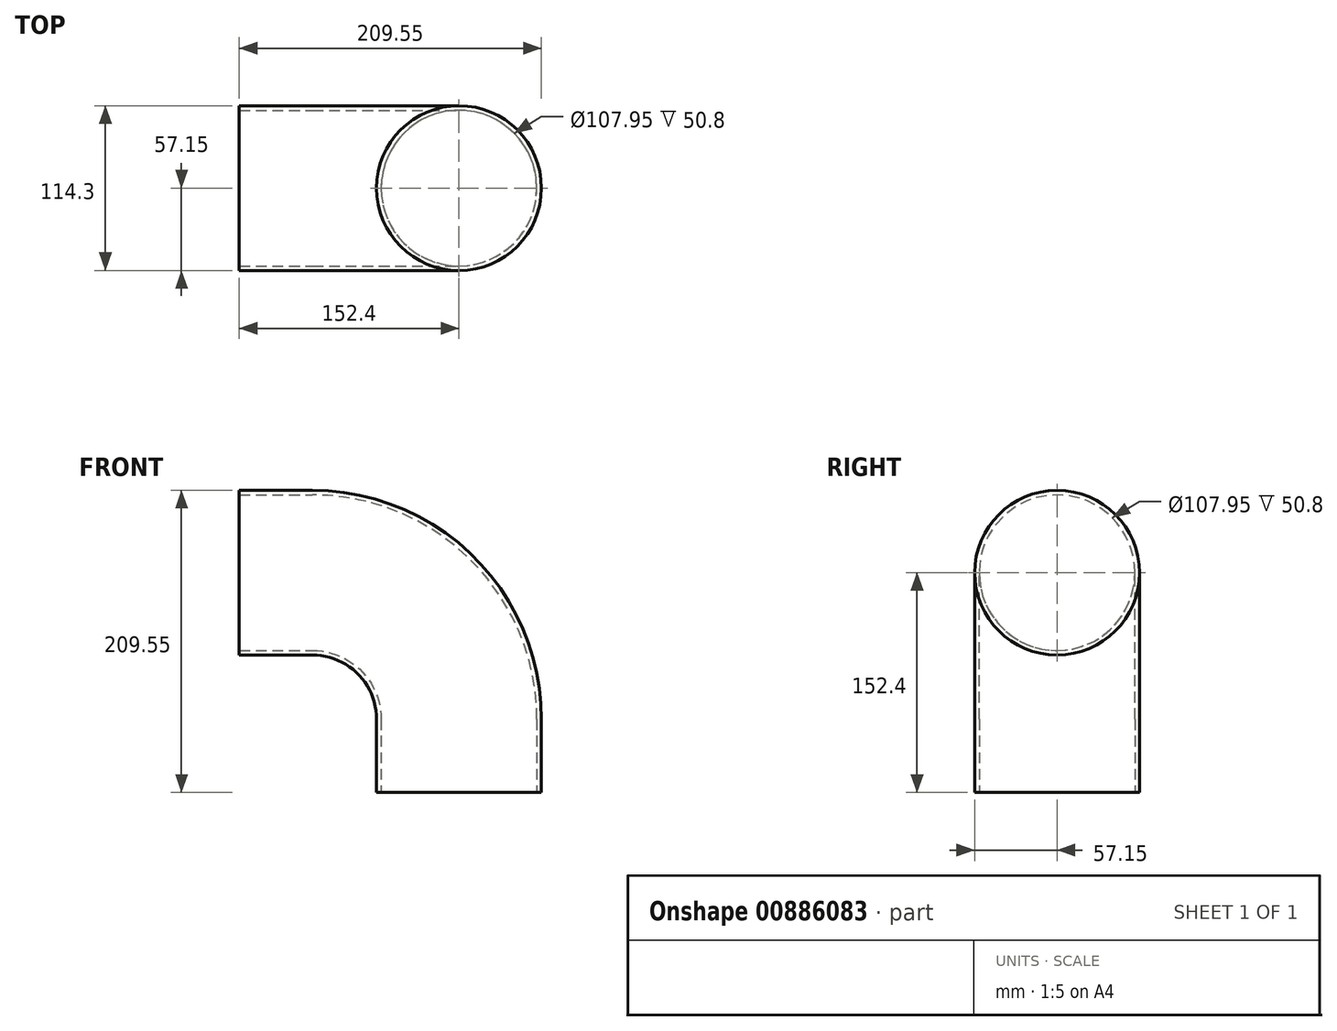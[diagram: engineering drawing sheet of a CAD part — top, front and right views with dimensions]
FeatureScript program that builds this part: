
annotation { "Feature Type Name" : "Feature", "Feature Type Description" : "" }
export const myFeature = defineFeature(function(context is Context, id is Id, definition is map)
    precondition{}
    {
        {
            var Q0;
            Q0=qCreatedBy(makeId("Front.planeOp"),FACE);
            var sketch = newSketch(context, id + "F0", { "sketchPlane" : qUnion([Q0])});
            skLineSegment(sketch, "E0", {"start": v(0, 0) * mm, "end": v(50.8, 0) * mm});
            skLineSegment(sketch, "E1", {"start": v(152.4, -101.6) * mm, "end": v(152.4, -152.4) * mm});
            skPoint(sketch, "E2.visualSharp", {"position": v(152.4, 0) * mm});
            skArc(sketch, "E2.filletArc", {"start": v(152.4, -101.6) * mm, "mid": v(122.64, -29.76) * mm, "end": v(50.8, 0) * mm});
            skSolve(sketch);
        }
        {
            var Q0;
            Q0=qCreatedBy(makeId("Right.planeOp"),FACE);
            var sketch = newSketch(context, id + "F1", { "sketchPlane" : qUnion([Q0])});
            skCircle(sketch, "E3", {"center": v(0, 0) * mm, "radius": 53.98 * mm});
            skCircle(sketch, "E4", {"center": v(0, 0) * mm, "radius": 57.15 * mm});
            skSolve(sketch);
        }
        {
            var Q0;
            Q0=makeQuery(id+"F1.imprint","IMPRINT",FACE,{"disambiguationData":[TD([[makeQuery(id+"F1.imprint","IMPRINT",EDGE,{"derivedFrom":sQuery(id+"F1.wireOp",EDGE,"E3")}),-1.0]])]});
            var Q1;
            Q1=sQuery(id+"F0.wireOp",EDGE,"E0");
            var Q2;
            Q2=sQuery(id+"F0.wireOp",EDGE,"E2.filletArc");
            var Q3;
            Q3=sQuery(id+"F0.wireOp",EDGE,"E1");
            sweep(context, id + "F2", {"profiles" : qUnion([Q0]), "path" : qUnion([Q1, Q2, Q3])});
        }
    });
